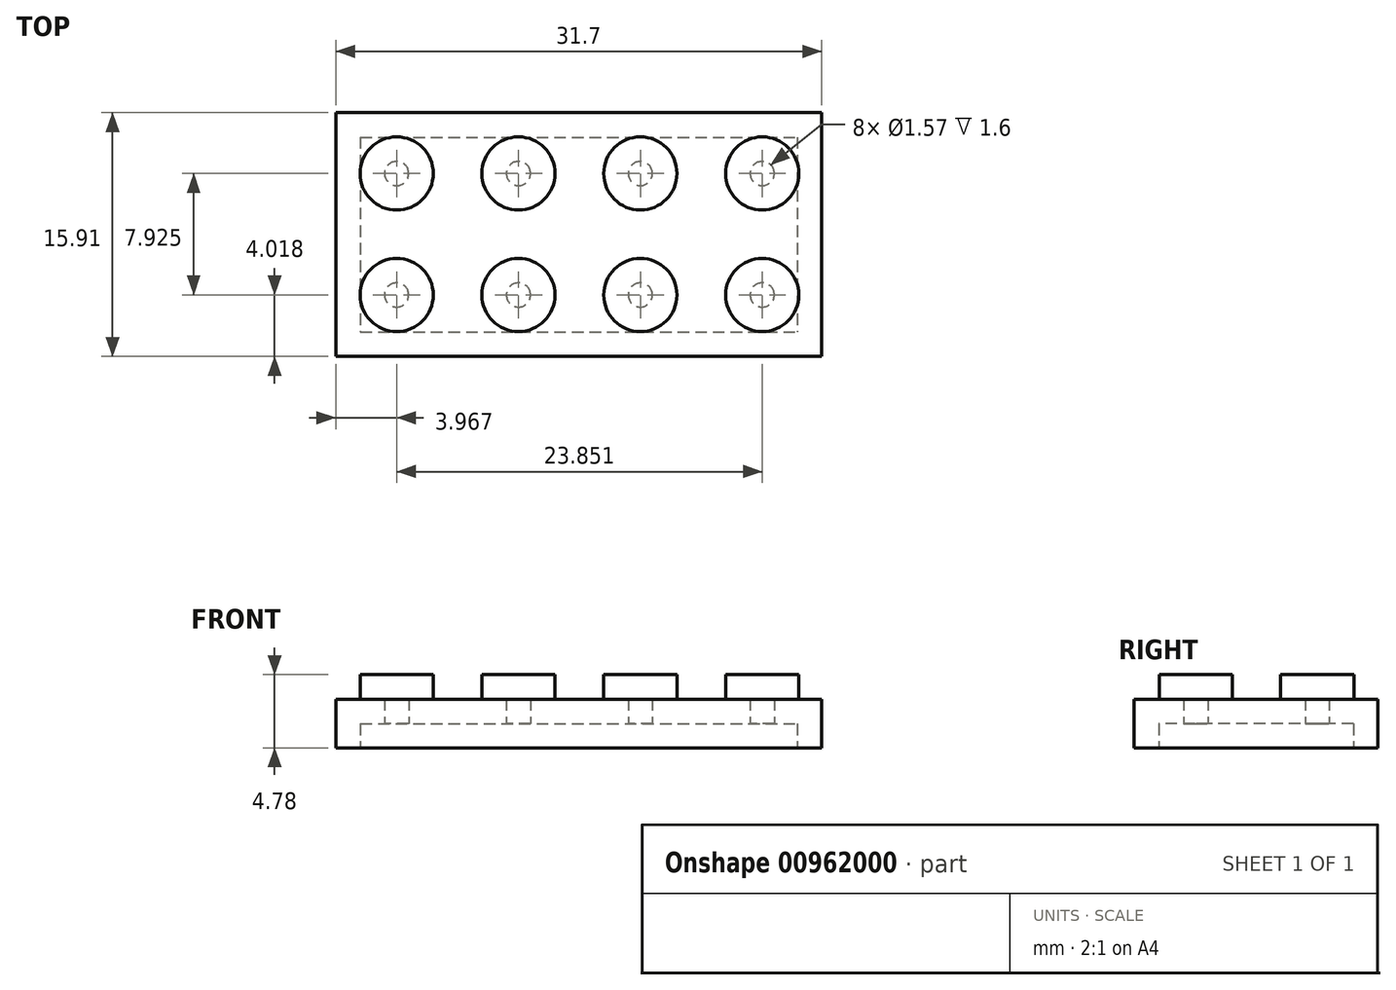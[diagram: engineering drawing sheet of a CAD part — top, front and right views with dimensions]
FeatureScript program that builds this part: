
annotation { "Feature Type Name" : "Feature", "Feature Type Description" : "" }
export const myFeature = defineFeature(function(context is Context, id is Id, definition is map)
    precondition{}
    {
        {
            var Q0;
            Q0=qCreatedBy(makeId("Top.planeOp"),FACE);
            var sketch = newSketch(context, id + "F0", { "sketchPlane" : qUnion([Q0])});
            skLineSegment(sketch, "E0.bottom", {"start": v(-15.34, 0.74) * mm, "end": v(16.36, 0.74) * mm});
            skLineSegment(sketch, "E0.top", {"start": v(-15.34, -15.17) * mm, "end": v(16.36, -15.17) * mm});
            skLineSegment(sketch, "E0.left", {"start": v(-15.34, 0.74) * mm, "end": v(-15.34, -15.17) * mm});
            skLineSegment(sketch, "E0.right", {"start": v(16.36, 0.74) * mm, "end": v(16.36, -15.17) * mm});
            skCircle(sketch, "E1", {"center": v(-11.37, -3.23) * mm, "radius": 2.39 * mm});
            skCircle(sketch, "E2.0.1.0", {"center": v(-11.37, -11.15) * mm, "radius": 2.39 * mm});
            skCircle(sketch, "E2.1.0.0", {"center": v(-3.42, -3.23) * mm, "radius": 2.39 * mm});
            skCircle(sketch, "E2.1.1.0", {"center": v(-3.42, -11.15) * mm, "radius": 2.39 * mm});
            skCircle(sketch, "E2.2.0.0", {"center": v(4.53, -3.23) * mm, "radius": 2.39 * mm});
            skCircle(sketch, "E2.2.1.0", {"center": v(4.53, -11.15) * mm, "radius": 2.39 * mm});
            skCircle(sketch, "E2.3.0.0", {"center": v(12.48, -3.23) * mm, "radius": 2.39 * mm});
            skCircle(sketch, "E2.3.1.0", {"center": v(12.48, -11.15) * mm, "radius": 2.39 * mm});
            skLineSegment(sketch, "E2.direction1", {"start": v(-11.37, -3.23) * mm, "end": v(-3.42, -3.23) * mm, "construction": true});
            skLineSegment(sketch, "E2.direction2", {"start": v(-11.37, -3.23) * mm, "end": v(-11.37, -11.15) * mm, "construction": true});
            skSolve(sketch);
        }
        {
            var Q0;
            Q0=makeQuery(id+"F0.imprint","IMPRINT",FACE,{"disambiguationData":[TD([[makeQuery(id+"F0.imprint","IMPRINT",EDGE,{"derivedFrom":sQuery(id+"F0.wireOp",EDGE,"E0.bottom")}),-1.0]])]});
            extrude(context, id + "F1", {"entities" : qUnion([Q0]), "depth" : 3.17 * mm, "offsetDistance" : 25.4 * mm});
        }
        {
            var Q0;
            Q0=makeQuery(id+"F0.imprint","IMPRINT",FACE,{"disambiguationData":[TD([[makeQuery(id+"F0.imprint","IMPRINT",EDGE,{"derivedFrom":sQuery(id+"F0.wireOp",EDGE,"E1")}),1.0]])]});
            var Q1;
            Q1=makeQuery(id+"F0.imprint","IMPRINT",FACE,{"disambiguationData":[TD([[makeQuery(id+"F0.imprint","IMPRINT",EDGE,{"derivedFrom":sQuery(id+"F0.wireOp",EDGE,"E2.1.0.0")}),1.0]])]});
            var Q2;
            Q2=makeQuery(id+"F0.imprint","IMPRINT",FACE,{"disambiguationData":[TD([[makeQuery(id+"F0.imprint","IMPRINT",EDGE,{"derivedFrom":sQuery(id+"F0.wireOp",EDGE,"E2.2.0.0")}),1.0]])]});
            var Q3;
            Q3=makeQuery(id+"F0.imprint","IMPRINT",FACE,{"disambiguationData":[TD([[makeQuery(id+"F0.imprint","IMPRINT",EDGE,{"derivedFrom":sQuery(id+"F0.wireOp",EDGE,"E2.3.0.0")}),1.0]])]});
            var Q4;
            Q4=makeQuery(id+"F0.imprint","IMPRINT",FACE,{"disambiguationData":[TD([[makeQuery(id+"F0.imprint","IMPRINT",EDGE,{"derivedFrom":sQuery(id+"F0.wireOp",EDGE,"E2.3.1.0")}),1.0]])]});
            var Q5;
            Q5=makeQuery(id+"F0.imprint","IMPRINT",FACE,{"disambiguationData":[TD([[makeQuery(id+"F0.imprint","IMPRINT",EDGE,{"derivedFrom":sQuery(id+"F0.wireOp",EDGE,"E2.2.1.0")}),1.0]])]});
            var Q6;
            Q6=makeQuery(id+"F0.imprint","IMPRINT",FACE,{"disambiguationData":[TD([[makeQuery(id+"F0.imprint","IMPRINT",EDGE,{"derivedFrom":sQuery(id+"F0.wireOp",EDGE,"E2.1.1.0")}),1.0]])]});
            var Q7;
            Q7=makeQuery(id+"F0.imprint","IMPRINT",FACE,{"disambiguationData":[TD([[makeQuery(id+"F0.imprint","IMPRINT",EDGE,{"derivedFrom":sQuery(id+"F0.wireOp",EDGE,"E2.0.1.0")}),1.0]])]});
            extrude(context, id + "F2", {"entities" : qUnion([Q0, Q1, Q2, Q3, Q4, Q5, Q6, Q7]), "operationType" : NewBodyOperationType.ADD, "depth" : 4.78 * mm, "offsetDistance" : 25.4 * mm});
        }
        {
            var Q0;
            {var subQ0=sQuery(id+"F0.wireOp",EDGE,"E2.3.1.0");var subQ1=sQuery(id+"F0.wireOp",EDGE,"E2.3.0.0");var subQ2=sQuery(id+"F0.wireOp",EDGE,"E2.2.1.0");var subQ3=sQuery(id+"F0.wireOp",EDGE,"E2.2.0.0");var subQ4=sQuery(id+"F0.wireOp",EDGE,"E2.1.1.0");var subQ5=sQuery(id+"F0.wireOp",EDGE,"E2.1.0.0");var subQ6=sQuery(id+"F0.wireOp",EDGE,"E2.0.1.0");var subQ7=sQuery(id+"F0.wireOp",EDGE,"E1");Q0=makeQuery(id+"F2.boolean.opBoolean","MERGE",FACE,{"derivedFrom":[makeQuery(id+"F1.opExtrude","CAP_FACE",FACE,{"disambiguationData":[OSD([sQuery(id+"F0.wireOp",EDGE,"E0.bottom"),sQuery(id+"F0.wireOp",EDGE,"E0.top"),sQuery(id+"F0.wireOp",EDGE,"E0.left"),sQuery(id+"F0.wireOp",EDGE,"E0.right"),subQ7,subQ6,subQ5,subQ4,subQ3,subQ2,subQ1,subQ0])],"isStart":true}),makeQuery(id+"F2.opExtrude","CAP_FACE",FACE,{"disambiguationData":[OSD([subQ7])],"isStart":true}),makeQuery(id+"F2.opExtrude","CAP_FACE",FACE,{"disambiguationData":[OSD([subQ6])],"isStart":true}),makeQuery(id+"F2.opExtrude","CAP_FACE",FACE,{"disambiguationData":[OSD([subQ5])],"isStart":true}),makeQuery(id+"F2.opExtrude","CAP_FACE",FACE,{"disambiguationData":[OSD([subQ4])],"isStart":true}),makeQuery(id+"F2.opExtrude","CAP_FACE",FACE,{"disambiguationData":[OSD([subQ3])],"isStart":true}),makeQuery(id+"F2.opExtrude","CAP_FACE",FACE,{"disambiguationData":[OSD([subQ2])],"isStart":true}),makeQuery(id+"F2.opExtrude","CAP_FACE",FACE,{"disambiguationData":[OSD([subQ1])],"isStart":true}),makeQuery(id+"F2.opExtrude","CAP_FACE",FACE,{"disambiguationData":[OSD([subQ0])],"isStart":true})]});}
            shell(context, id + "F3", {"entities" : qUnion([Q0]), "thickness" : 1.6 * mm});
        }
    });
